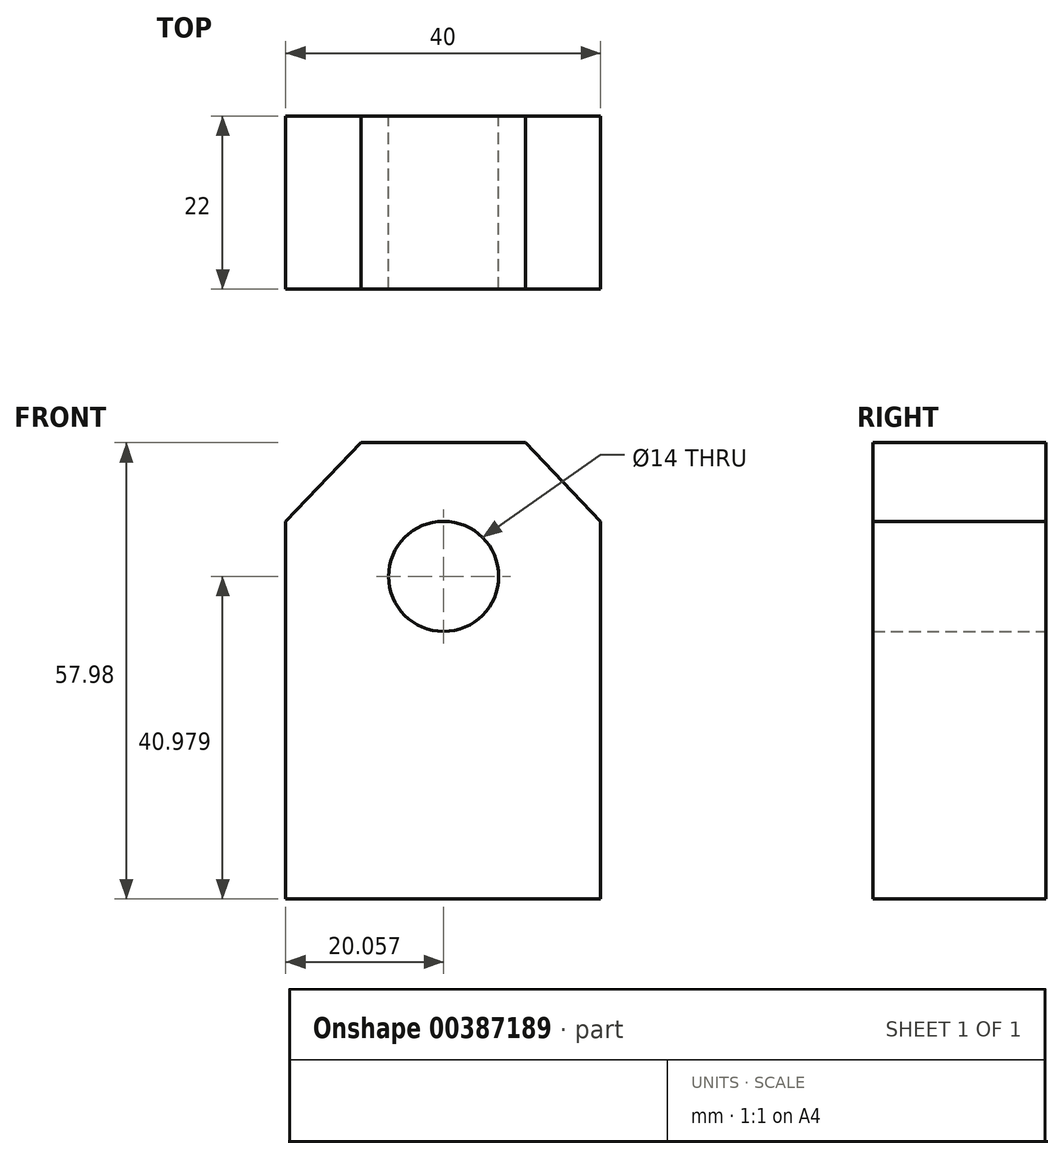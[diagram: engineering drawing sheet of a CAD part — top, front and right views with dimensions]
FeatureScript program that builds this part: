
annotation { "Feature Type Name" : "Feature", "Feature Type Description" : "" }
export const myFeature = defineFeature(function(context is Context, id is Id, definition is map)
    precondition{}
    {
        {
            var Q0;
            Q0=qCreatedBy(makeId("Front.planeOp"),FACE);
            var sketch = newSketch(context, id + "F0", { "sketchPlane" : qUnion([Q0])});
            skLineSegment(sketch, "E0.bottom", {"start": v(10.46, 29) * mm, "end": v(-10.46, 29) * mm});
            skLineSegment(sketch, "E0.top", {"start": v(20, -29) * mm, "end": v(-20, -29) * mm});
            skLineSegment(sketch, "E0.left", {"start": v(20, 18.99) * mm, "end": v(20, -29) * mm});
            skLineSegment(sketch, "E0.right", {"start": v(-20, 18.99) * mm, "end": v(-20, -29) * mm});
            skPoint(sketch, "E0.middle", {"position": v(0, 0) * mm});
            skPoint(sketch, "E1", {"position": v(20, 18.99) * mm});
            skLineSegment(sketch, "E2", {"start": v(20, 18.99) * mm, "end": v(10.46, 29) * mm});
            skCircle(sketch, "E3", {"center": v(0.06, 11.99) * mm, "radius": 7 * mm});
            skPoint(sketch, "E3.first.point", {"position": v(0, 18.99) * mm});
            skPoint(sketch, "E3.second.point", {"position": v(0, 5) * mm});
            skPoint(sketch, "E3.second.point.positionSnap0", {"position": v(0, 18.99) * mm});
            skPoint(sketch, "E3.third.point", {"position": v(-1.3, 5.12) * mm});
            skLineSegment(sketch, "E4.MirrorCS", {"start": v(-20, 18.99) * mm, "end": v(-10.46, 29) * mm});
            skSolve(sketch);
        }
        {
            var Q0;
            Q0 = qSketchRegion(id + "F0", true);
            extrude(context, id + "F1", {"entities" : qUnion([Q0]), "depth" : 22 * mm});
        }
    });
